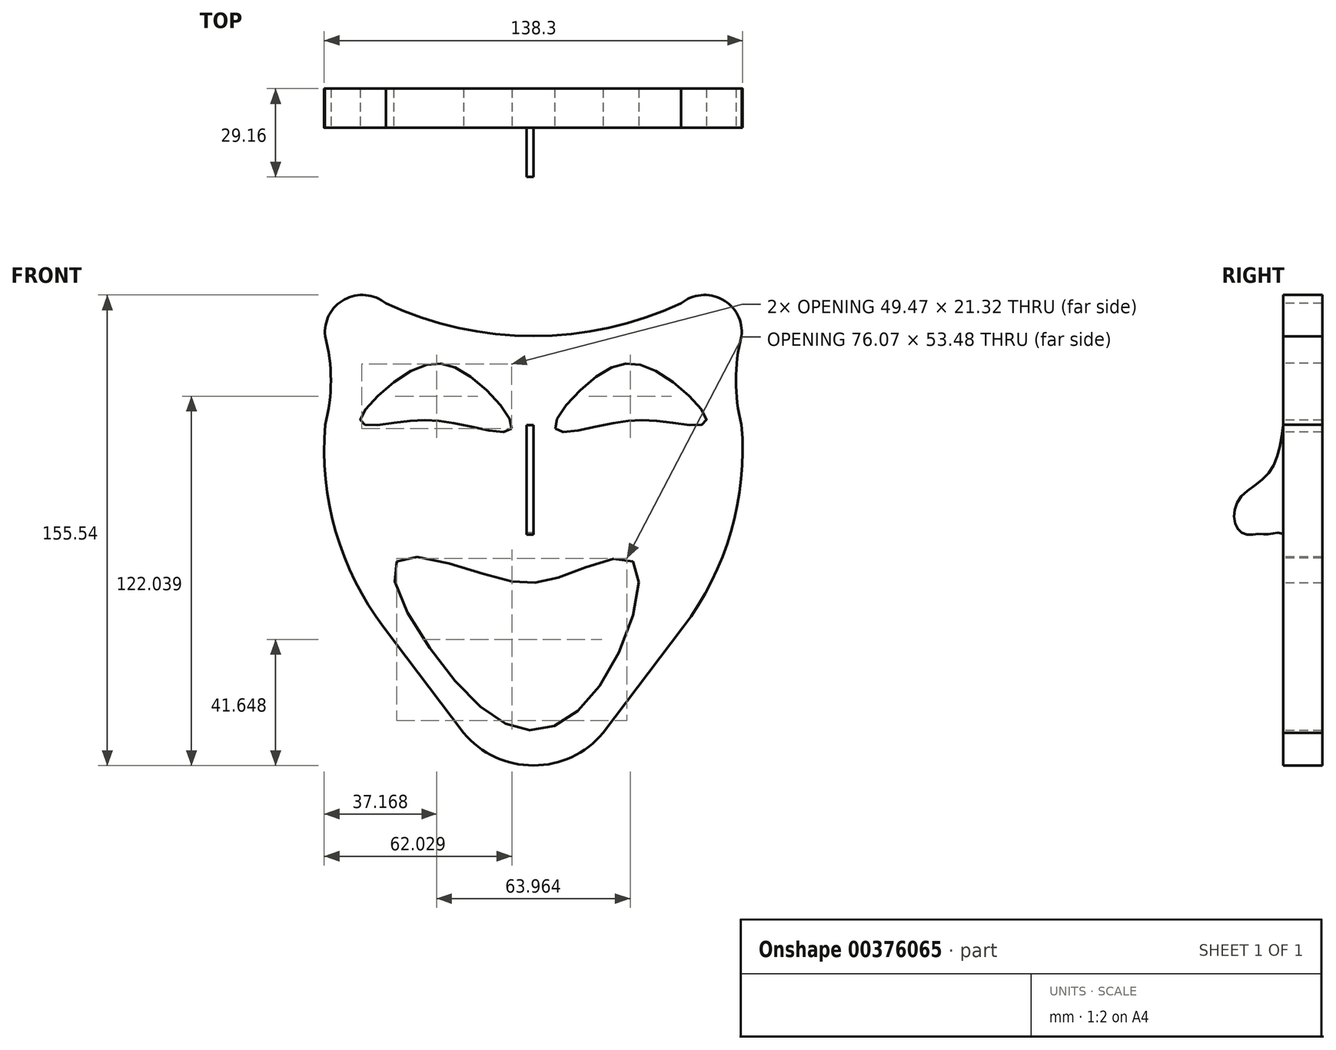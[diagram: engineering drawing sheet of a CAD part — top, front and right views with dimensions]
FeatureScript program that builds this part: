
annotation { "Feature Type Name" : "Feature", "Feature Type Description" : "" }
export const myFeature = defineFeature(function(context is Context, id is Id, definition is map)
    precondition{}
    {
        {
            var Q0;
            Q0=qCreatedBy(makeId("Front.planeOp"),FACE);
            var sketch = newSketch(context, id + "F0", { "sketchPlane" : qUnion([Q0])});
            skArc(sketch, "E0", {"start": v(-48.8, 76.22) * mm, "mid": v(0, 65.38) * mm, "end": v(48.8, 76.22) * mm});
            skArc(sketch, "E1", {"start": v(-48.8, 76.22) * mm, "mid": v(-62.45, 77.53) * mm, "end": v(-68.8, 65.38) * mm});
            skPoint(sketch, "E1.endSnap0", {"position": v(0, 65.38) * mm});
            skArc(sketch, "E2", {"start": v(-68.8, 36.08) * mm, "mid": v(-66.93, 50.73) * mm, "end": v(-68.8, 65.38) * mm});
            skArc(sketch, "E3", {"start": v(-68.8, 36.08) * mm, "mid": v(-65.33, 0.82) * mm, "end": v(-49.46, -30.85) * mm});
            skLineSegment(sketch, "E4", {"start": v(-49.46, -30.85) * mm, "end": v(-23.03, -65.78) * mm});
            skLineSegment(sketch, "E5", {"start": v(0, 65.38) * mm, "end": v(0, -76.53) * mm, "construction": true});
            skArc(sketch, "E6.MirrorCS", {"start": v(48.8, 76.22) * mm, "mid": v(62.45, 77.53) * mm, "end": v(68.8, 65.38) * mm});
            skArc(sketch, "E7.MirrorCS", {"start": v(68.8, 36.08) * mm, "mid": v(66.93, 50.73) * mm, "end": v(68.8, 65.38) * mm});
            skArc(sketch, "E8.MirrorCS", {"start": v(68.8, 36.08) * mm, "mid": v(65.33, 0.82) * mm, "end": v(49.46, -30.85) * mm});
            skLineSegment(sketch, "E9.MirrorCS", {"start": v(49.46, -30.85) * mm, "end": v(23.03, -65.78) * mm});
            skArc(sketch, "E10", {"start": v(-23.03, -65.78) * mm, "mid": v(0, -76.53) * mm, "end": v(23.03, -65.78) * mm});
            skFitSpline(sketch, "E11", {"points": [v(-7.25, 34.85) * mm, v(-22.03, 52.87) * mm, v(-40.5, 53.79) * mm, v(-57.14, 37.16) * mm, v(-42.82, 37.16) * mm, v(-24.21, 36.22) * mm, v(-7.25, 34.85) * mm]});
            skFitSpline(sketch, "E12.MirrorC", {"points": [v(7.25, 34.85) * mm, v(22.03, 52.87) * mm, v(40.5, 53.79) * mm, v(57.14, 37.16) * mm, v(42.82, 37.16) * mm, v(24.21, 36.22) * mm, v(7.25, 34.85) * mm]});
            skFitSpline(sketch, "E13", {"points": [v(-45.16, -9.07) * mm, v(-13.04, -14.25) * mm, v(8.92, -14.25) * mm, v(32.8, -9.07) * mm, v(24.65, -46) * mm, v(0, -64.94) * mm, v(-28.04, -46) * mm, v(-45.16, -9.07) * mm]});
            skSolve(sketch);
        }
        {
            var Q0;
            Q0=makeQuery(id+"F0.imprint","IMPRINT",FACE,{"disambiguationData":[TD([[makeQuery(id+"F0.imprint","IMPRINT",EDGE,{"derivedFrom":sQuery(id+"F0.wireOp",EDGE,"E0")}),-1.0]])]});
            extrude(context, id + "F1", {"entities" : qUnion([Q0]), "oppositeDirection" : true, "depth" : 12.95 * mm});
        }
        {
            var Q0;
            Q0=qCreatedBy(makeId("Right.planeOp"),FACE);
            var sketch = newSketch(context, id + "F2", { "sketchPlane" : qUnion([Q0])});
            skFitSpline(sketch, "E14", {"points": [v(0, 35.93) * mm, v(-4.66, 20.26) * mm, v(-14.1, 12) * mm, v(-16.02, 4.24) * mm, v(-12.89, 0) * mm, v(-7.78, 0) * mm, v(-4.09, 0) * mm, v(0, 0) * mm], "startDerivative": vector(-9.04, -84.87) * mm, "endDerivative": vector(39.37, -26.98) * mm});
            skLineSegment(sketch, "E15", {"start": v(0, 35.93) * mm, "end": v(0, 0) * mm});
            skSolve(sketch);
        }
        {
            var Q0;
            Q0=makeQuery(id+"F2.imprint","IMPRINT",FACE,{"disambiguationData":[TD([[makeQuery(id+"F2.imprint","IMPRINT",EDGE,{"derivedFrom":sQuery(id+"F2.wireOp",EDGE,"E14")}),1.0]])]});
            extrude(context, id + "F3", {"entities" : qUnion([Q0]), "operationType" : NewBodyOperationType.ADD, "oppositeDirection" : true, "depth" : 2.3 * mm});
        }
    });
